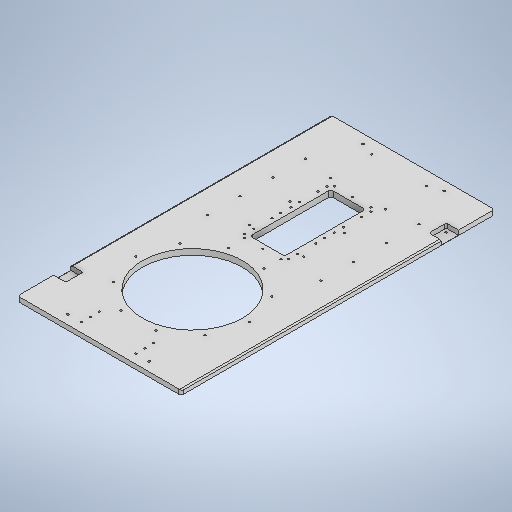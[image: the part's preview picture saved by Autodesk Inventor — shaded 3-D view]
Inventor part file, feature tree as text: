
AUTODESK INVENTOR PART (.ipt)
format: ipt  version: 2025 (Build 290162000, 162)  size: 637,952 bytes
history: native  units: in
note: dims shown in document units (in); Inventor stores cm internally (conversion verified against a paired STEP export)
features: sketch x17, extrude x6, hole x5, fillet x3, chamfer x3, plane x2
ambient origin geometry x8: Origin, YZ Plane, XZ Plane, XY Plane, X Axis, Y Axis, Z Axis, Center Point
bodies: Solid1 (feature_tree)
feature tree (36):
  extrude  "Base Cover"  Depth=14.1732in
  sketch  "Sketch2"  dims[d5=8.6614in d6=0.0in d7=0.0in]
  extrude  "Cylinder Hole"  Depth=0.503in
  plane  "Work Plane1"
  hole  "Hole3"  [1 undecoded]
  sketch  "Sketch7"  dims[d69=0.1575in d70=3.937in d72=360.0deg]
  plane  "Work Plane2"
  hole  "Hole4"  [1 undecoded]
  sketch  "Sketch9"  dims[d82=1.063in]
  fillet  "Rounded Side Corners"  Radius=7.0625in
  chamfer  "Chamfer1"  Distance=3.937in Angle=360.0deg
  chamfer  "Chamfer2"  Distance=0.1969in
  extrude  "Magnet Seats"  Depth=0.3937in TaperAngle=45.0deg
  hole  "Hole5"  [1 undecoded]
  chamfer  "Chamfer5"  Distance=0.1181in
  hole  "Hole6"  [1 undecoded]
  sketch  "Sketch15"  dims[d85=1.4961in]
  extrude  "Extrusion11"  Depth=0.3937in TaperAngle=0.0deg
  fillet  "Fillet3"  Radius=0.748in
  hole  "Hole7"  [1 undecoded]
  fillet  "Rounded Bottom Corners"  Radius=0.8661in
  extrude  "Extrusion14"  Depth=0.3937in
  extrude  "Extrusion15"  Depth=0.3937in
  sketch  "Sketch1"  dims[d0=14.1732in d1=27.1654in]
  sketch  "Sketch6"  dims[d68=9.8425in]
  sketch  "Sketch8"  dims[d74=0.1628in d75=0.3937in d76=0.1575in d77=0.0787in d78=90.0deg d79=0.3937in d80=0.8108in]
  sketch  "Sketch Circular Pattern4"  dims[d57=0.1936in d58=0.1969in d59=0.1575in d60=0.0787in d61=90.0deg d62=0.1969in d63=0.8108in]
  sketch  "Sketch11"  dims[d83=1.063in]
  sketch  "Sketch12"  dims[d84=1.4961in]
  sketch  "Sketch Rectangular Pattern1"  dims[d2=0.503in d3=0.0in d4=8.0709in]
  sketch  "Sketch Rectangular Pattern2"  dims[d8=10.6299in d50=5.9055in d55=7.0625in]
  sketch  "Sketch Rectangular Pattern3"  dims[d56=25.5906in]
  sketch  "Sketch Rectangular Pattern4"  dims[d64=10.3543in]
  sketch  "Sketch Rectangular Pattern5"  dims[d65=10.6299in]
  sketch  "Sketch18"  dims[d86=3.1102in]
  sketch  "Sketch19"  dims[d87=3.1102in d88=0.1969in d89=0.0984in d90=0.0787in d91=45.0deg d92=0.0984in d93=0.0787in d94=45.0deg d95=0.1181in d96=0.1181in d97=0.3848in d98=0.0in d109=0.748in d110=0.315in d111=0.8661in d112=0.748in d113=0.1299in d114=0.1299in d115=0.1299in d116=0.1299in d118=0.315in d119=0.8661in d120=0.748in d121=0.748in d122=0.1276in d123=0.315in d124=0.1575in d125=0.0787in d126=90.0deg d127=0.315in d128=0.8108in d129=0.0138in d130=0.0787in d131=45.0deg d146=3.9469in d147=0.7874in d148=0.3937in d149=0.1575in d150=3.937in d152=1.1811in d153=0.3937in d155=0.3937in d157=0.1575in d158=1.1811in d160=0.7874in d161=0.3937in d163=0.3937in d165=9.8425in d166=0.1575in d167=2.9528in d168=1.1811in d169=3.1496in d171=1.4173in d172=0.3937in d174=0.3937in d176=0.1628in d177=0.3937in d178=0.1575in d179=0.0787in d180=90.0deg d181=0.3937in d182=0.8108in d191=3.0in d192=7.0in d193=6.4961in d194=0.8312in d195=0.0in d196=0.1969in d197=0.3937in d198=0.1969in d199=1.9685in d201=0.7874in d202=0.3937in d204=0.3937in d206=0.3189in d207=0.1969in d208=0.3189in d209=1.9685in d211=0.7874in d212=0.3937in d214=0.3937in d216=0.1628in d217=0.3937in d218=0.1575in d219=0.0787in d220=90.0deg d221=0.3937in d222=0.8108in d230=0.2756in d243=0.1378in d244=0.0787in d245=0.3848in d246=0.0in d247=0.1378in d248=0.0787in d249=0.3937in d250=0.0in d26=0.0394in d27=0.0394in d28=0.0394in d29=0.0059in d30=0.0098in d31=0.0148in d32=0.5635in d33=0.0295in d34=0.8108in d35=0.0025in d36=0.0295in d37=0.0148in d66=0.0197in d67=0.0344in]
note: 5 required parameter values undecoded (feature->parameter linkage not recoverable at this tier; creation-order binding heuristic only, values carry confidence <= 0.55)
